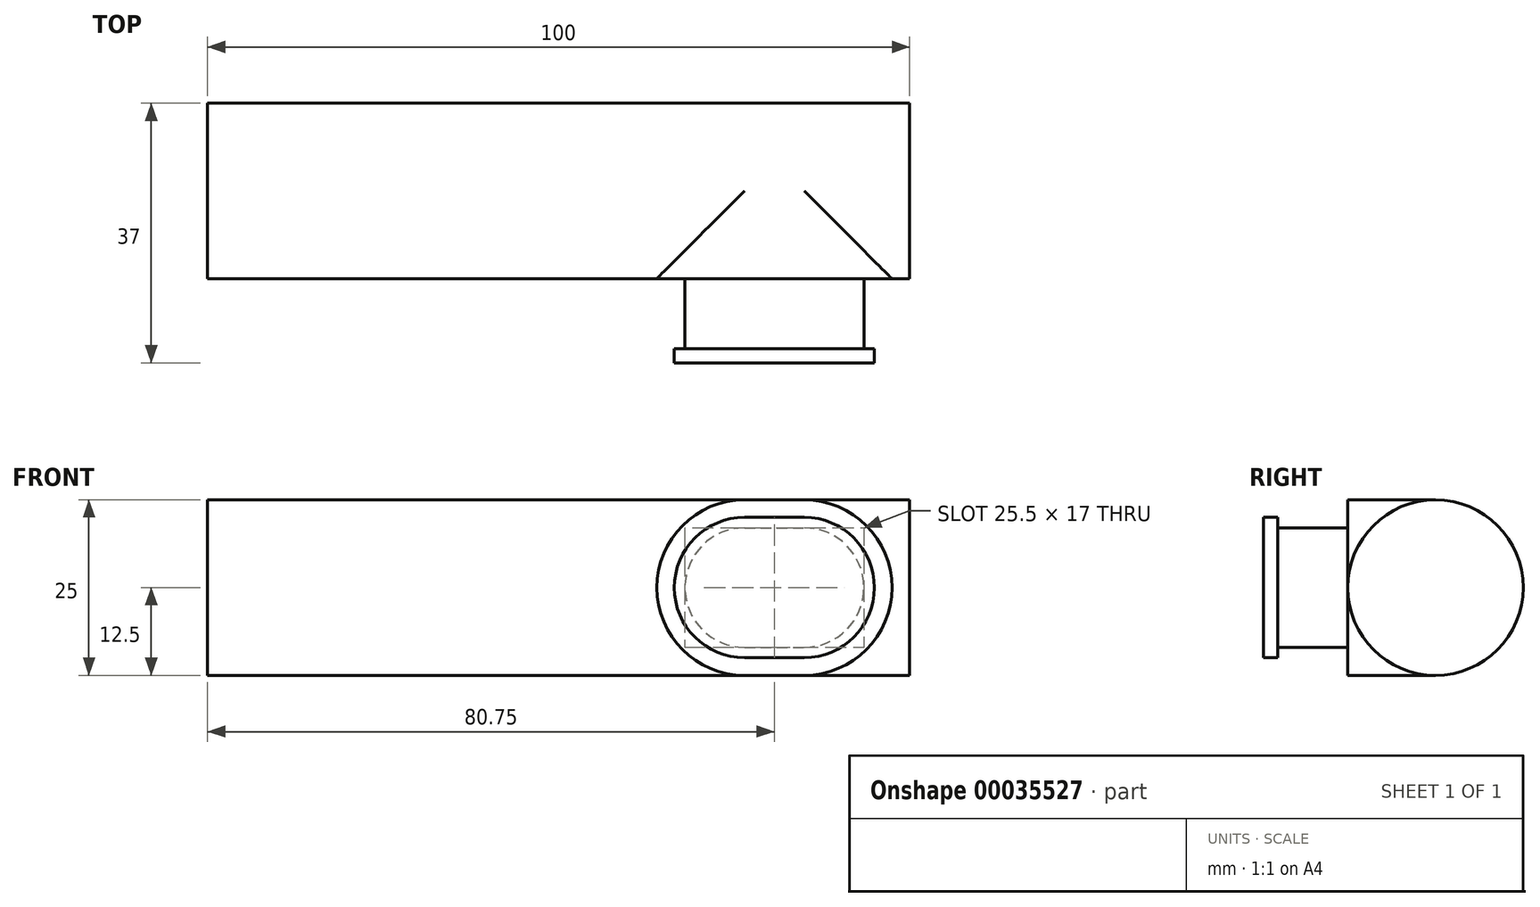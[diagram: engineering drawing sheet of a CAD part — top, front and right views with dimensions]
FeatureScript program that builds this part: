
annotation { "Feature Type Name" : "Feature", "Feature Type Description" : "" }
export const myFeature = defineFeature(function(context is Context, id is Id, definition is map)
    precondition{}
    {
        {
            var Q0;
            Q0=qCreatedBy(makeId("Right.planeOp"),FACE);
            var sketch = newSketch(context, id + "F0", { "sketchPlane" : qUnion([Q0])});
            skCircle(sketch, "E0", {"center": v(0, 0) * mm, "radius": 12.5 * mm});
            skSolve(sketch);
        }
        {
            var Q0;
            Q0=makeQuery(id+"F0.imprint","IMPRINT",FACE,{"disambiguationData":[TD([[makeQuery(id+"F0.imprint","IMPRINT",EDGE,{"derivedFrom":sQuery(id+"F0.wireOp",EDGE,"E0")}),1.0]])]});
            extrude(context, id + "F1", {"entities" : qUnion([Q0]), "endBound" : BoundingType.SYMMETRIC, "depth" : 100 * mm});
        }
        {
            var Q0;
            Q0=qCreatedBy(makeId("Front.planeOp"),FACE);
            var sketch = newSketch(context, id + "F2", { "sketchPlane" : qUnion([Q0])});
            skLineSegment(sketch, "E1", {"start": v(26.5, 12.5) * mm, "end": v(35, 12.5) * mm});
            skLineSegment(sketch, "E2", {"start": v(26.5, -12.5) * mm, "end": v(35, -12.5) * mm});
            skArc(sketch, "E3", {"start": v(35, -12.5) * mm, "mid": v(47.5, 0) * mm, "end": v(35, 12.5) * mm});
            skArc(sketch, "E4", {"start": v(26.5, -12.5) * mm, "mid": v(14, 0) * mm, "end": v(26.5, 12.5) * mm});
            skSolve(sketch);
        }
        {
            var Q0;
            Q0 = qSketchRegion(id + "F2", true);
            extrude(context, id + "F3", {"entities" : qUnion([Q0]), "operationType" : NewBodyOperationType.ADD, "depth" : 12.5 * mm});
        }
        {
            var Q0;
            Q0=makeQuery(id+"F3.opExtrude","CAP_FACE",FACE,{"disambiguationData":[OSD([sQuery(id+"F2.wireOp",EDGE,"E1"),sQuery(id+"F2.wireOp",EDGE,"E2"),sQuery(id+"F2.wireOp",EDGE,"E3"),sQuery(id+"F2.wireOp",EDGE,"E4")])],"isStart":false});
            var sketch = newSketch(context, id + "F4", { "sketchPlane" : qUnion([Q0])});
            skLineSegment(sketch, "E5", {"start": v(26.5, 8.5) * mm, "end": v(35, 8.5) * mm});
            skLineSegment(sketch, "E6", {"start": v(26.5, -8.5) * mm, "end": v(35, -8.5) * mm});
            skArc(sketch, "E7", {"start": v(35, -8.5) * mm, "mid": v(43.5, 0) * mm, "end": v(35, 8.5) * mm});
            skArc(sketch, "E8", {"start": v(26.5, -8.5) * mm, "mid": v(18, 0) * mm, "end": v(26.5, 8.5) * mm});
            skSolve(sketch);
        }
        {
            var Q0;
            Q0 = qSketchRegion(id + "F4", true);
            extrude(context, id + "F5", {"entities" : qUnion([Q0]), "operationType" : NewBodyOperationType.ADD, "depth" : 10 * mm});
        }
        {
            var Q0;
            Q0=makeQuery(id+"F5.opExtrude","CAP_FACE",FACE,{"disambiguationData":[OSD([sQuery(id+"F4.wireOp",EDGE,"E5"),sQuery(id+"F4.wireOp",EDGE,"E6"),sQuery(id+"F4.wireOp",EDGE,"E7"),sQuery(id+"F4.wireOp",EDGE,"E8")])],"isStart":false});
            var sketch = newSketch(context, id + "F6", { "sketchPlane" : qUnion([Q0])});
            skLineSegment(sketch, "E9", {"start": v(26.5, 10) * mm, "end": v(35, 10) * mm});
            skLineSegment(sketch, "E10", {"start": v(26.5, -10) * mm, "end": v(35, -10) * mm});
            skArc(sketch, "E11", {"start": v(35, -10) * mm, "mid": v(45, 0) * mm, "end": v(35, 10) * mm});
            skArc(sketch, "E12", {"start": v(26.5, -10) * mm, "mid": v(16.5, 0) * mm, "end": v(26.5, 10) * mm});
            skSolve(sketch);
        }
        {
            var Q0;
            Q0 = qSketchRegion(id + "F6", true);
            extrude(context, id + "F7", {"entities" : qUnion([Q0]), "operationType" : NewBodyOperationType.ADD, "depth" : 2 * mm});
        }
    });
